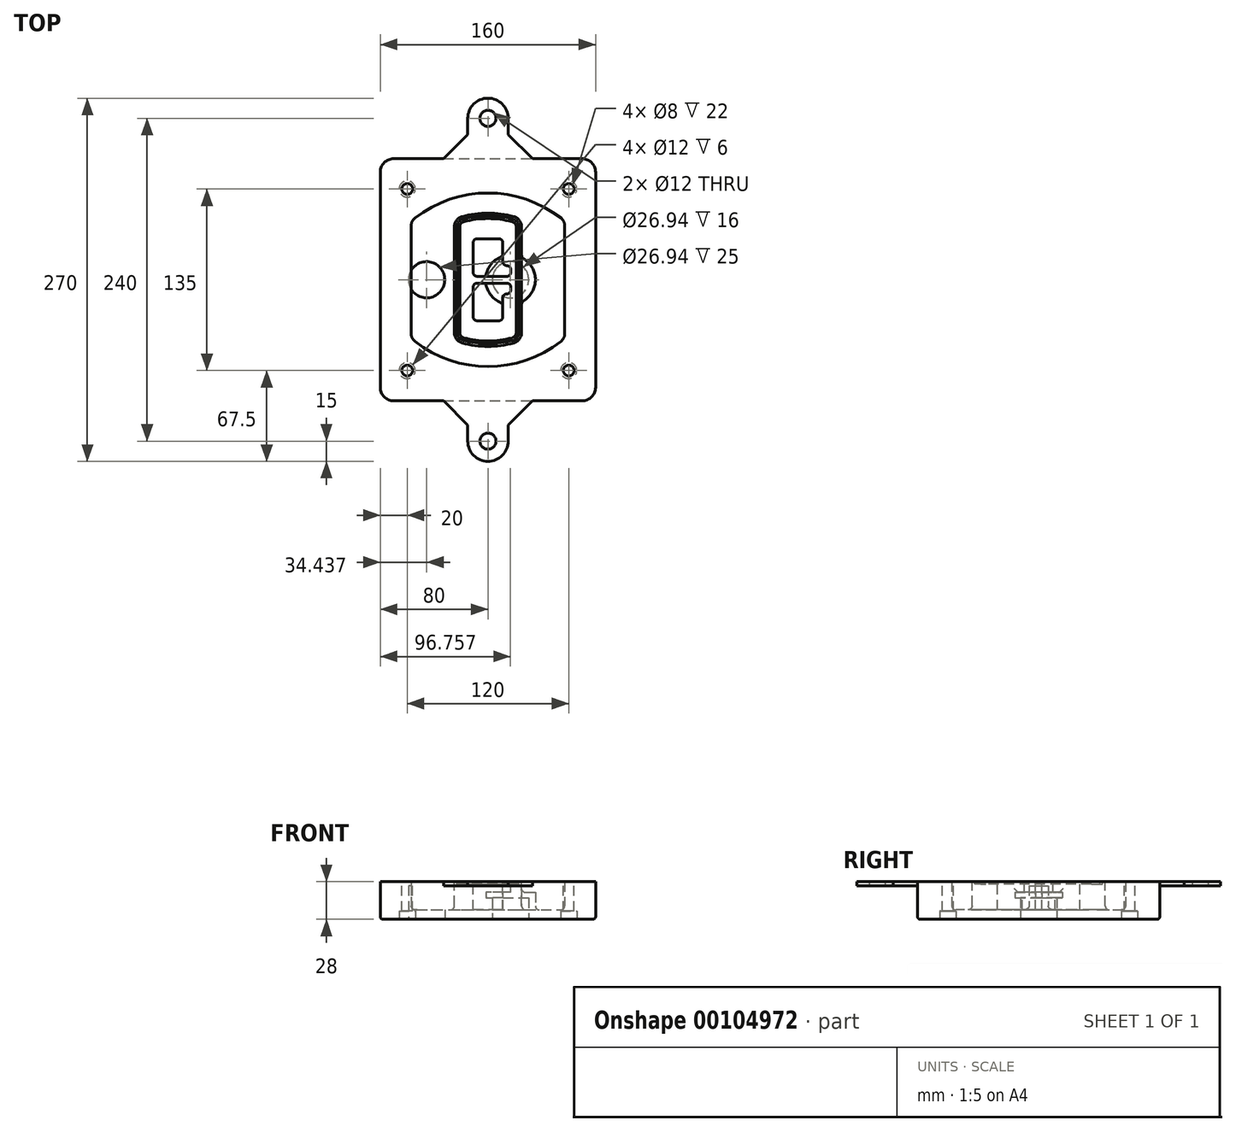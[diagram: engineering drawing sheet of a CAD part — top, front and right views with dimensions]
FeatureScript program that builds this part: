
annotation { "Feature Type Name" : "Feature", "Feature Type Description" : "" }
export const myFeature = defineFeature(function(context is Context, id is Id, definition is map)
    precondition{}
    {
        {
            var Q0;
            Q0=qCreatedBy(makeId("Top.planeOp"),FACE);
            var sketch = newSketch(context, id + "F0", { "sketchPlane" : qUnion([Q0])});
            skPoint(sketch, "E0.rect.middle", {"position": v(0, 0) * mm});
            skLineSegment(sketch, "E1.bottom", {"start": v(-70, -90) * mm, "end": v(70, -90) * mm});
            skLineSegment(sketch, "E1.top", {"start": v(-70, 90) * mm, "end": v(70, 90) * mm});
            skLineSegment(sketch, "E1.left", {"start": v(-80, -80) * mm, "end": v(-80, 80) * mm});
            skLineSegment(sketch, "E1.right", {"start": v(80, -80) * mm, "end": v(80, 80) * mm});
            skLineSegment(sketch, "E2", {"start": v(-80, 90) * mm, "end": v(80, -90) * mm, "construction": true});
            skLineSegment(sketch, "E3", {"start": v(80, 90) * mm, "end": v(-80, -90) * mm, "construction": true});
            skCircle(sketch, "E4", {"center": v(-60, 67.5) * mm, "radius": 4 * mm});
            skCircle(sketch, "E5", {"center": v(60, 67.5) * mm, "radius": 4 * mm});
            skCircle(sketch, "E6", {"center": v(60, -67.5) * mm, "radius": 4 * mm});
            skCircle(sketch, "E7", {"center": v(-60, -67.5) * mm, "radius": 4 * mm});
            skLineSegment(sketch, "E8", {"start": v(-60, 67.5) * mm, "end": v(60, 67.5) * mm, "construction": true});
            skLineSegment(sketch, "E9", {"start": v(60, 67.5) * mm, "end": v(60, -67.5) * mm, "construction": true});
            skLineSegment(sketch, "E10", {"start": v(60, -67.5) * mm, "end": v(-60, -67.5) * mm, "construction": true});
            skLineSegment(sketch, "E11", {"start": v(-60, -67.5) * mm, "end": v(-60, 67.5) * mm, "construction": true});
            skLineSegment(sketch, "E12", {"start": v(-60, 40.3) * mm, "end": v(-60, -40.3) * mm});
            skLineSegment(sketch, "E13", {"start": v(60, 40.3) * mm, "end": v(60, -40.3) * mm});
            skArc(sketch, "E14", {"start": v(56.15, 48.18) * mm, "mid": v(0, 67.5) * mm, "end": v(-56.15, 48.18) * mm});
            skArc(sketch, "E15", {"start": v(-56.15, -48.18) * mm, "mid": v(0, -67.5) * mm, "end": v(56.15, -48.18) * mm});
            skLineSegment(sketch, "E16", {"start": v(-60, 0) * mm, "end": v(60, 0) * mm, "construction": true});
            skPoint(sketch, "E17.visualSharp", {"position": v(-60, -45) * mm});
            skArc(sketch, "E17.filletArc", {"start": v(-60, -40.3) * mm, "mid": v(-58.99, -44.68) * mm, "end": v(-56.15, -48.18) * mm});
            skPoint(sketch, "E18.visualSharp", {"position": v(-60, 45) * mm});
            skArc(sketch, "E18.filletArc", {"start": v(-56.15, 48.18) * mm, "mid": v(-58.99, 44.68) * mm, "end": v(-60, 40.3) * mm});
            skPoint(sketch, "E19.visualSharp", {"position": v(60, 45) * mm});
            skArc(sketch, "E19.filletArc", {"start": v(60, 40.3) * mm, "mid": v(58.99, 44.68) * mm, "end": v(56.15, 48.18) * mm});
            skPoint(sketch, "E20.visualSharp", {"position": v(60, -45) * mm});
            skArc(sketch, "E20.filletArc", {"start": v(56.15, -48.18) * mm, "mid": v(58.99, -44.68) * mm, "end": v(60, -40.3) * mm});
            skPoint(sketch, "E21.visualSharp", {"position": v(-80, 90) * mm});
            skArc(sketch, "E21.filletArc", {"start": v(-70, 90) * mm, "mid": v(-77.07, 87.07) * mm, "end": v(-80, 80) * mm});
            skPoint(sketch, "E22.visualSharp", {"position": v(80, 90) * mm});
            skArc(sketch, "E22.filletArc", {"start": v(80, 80) * mm, "mid": v(77.07, 87.07) * mm, "end": v(70, 90) * mm});
            skPoint(sketch, "E23.visualSharp", {"position": v(80, -90) * mm});
            skArc(sketch, "E23.filletArc", {"start": v(70, -90) * mm, "mid": v(77.07, -87.07) * mm, "end": v(80, -80) * mm});
            skPoint(sketch, "E24.visualSharp", {"position": v(-80, -90) * mm});
            skArc(sketch, "E24.filletArc", {"start": v(-80, -80) * mm, "mid": v(-77.07, -87.07) * mm, "end": v(-70, -90) * mm});
            skArc(sketch, "E25.0", {"start": v(57, 40.3) * mm, "mid": v(56.3, 43.36) * mm, "end": v(54.3, 45.81) * mm});
            skLineSegment(sketch, "E25.1", {"start": v(57, 40.3) * mm, "end": v(57, -40.3) * mm});
            skArc(sketch, "E25.2", {"start": v(54.3, -45.81) * mm, "mid": v(56.3, -43.36) * mm, "end": v(57, -40.3) * mm});
            skArc(sketch, "E25.3", {"start": v(-54.3, -45.81) * mm, "mid": v(0, -64.5) * mm, "end": v(54.3, -45.81) * mm});
            skArc(sketch, "E25.4", {"start": v(-57, -40.3) * mm, "mid": v(-56.3, -43.36) * mm, "end": v(-54.3, -45.81) * mm});
            skArc(sketch, "E25.5", {"start": v(54.3, 45.81) * mm, "mid": v(0, 64.5) * mm, "end": v(-54.3, 45.81) * mm});
            skLineSegment(sketch, "E25.6", {"start": v(-57, 40.3) * mm, "end": v(-57, -40.3) * mm});
            skArc(sketch, "E25.7", {"start": v(-54.3, 45.81) * mm, "mid": v(-56.3, 43.36) * mm, "end": v(-57, 40.3) * mm});
            skArc(sketch, "E26.0", {"start": v(-58.62, 51.33) * mm, "mid": v(-62.58, 46.43) * mm, "end": v(-64, 40.3) * mm});
            skArc(sketch, "E26.1", {"start": v(58.62, 51.33) * mm, "mid": v(0, 71.5) * mm, "end": v(-58.62, 51.33) * mm});
            skArc(sketch, "E26.2", {"start": v(64, 40.3) * mm, "mid": v(62.58, 46.43) * mm, "end": v(58.62, 51.33) * mm});
            skLineSegment(sketch, "E26.3", {"start": v(64, 40.3) * mm, "end": v(64, -40.3) * mm});
            skArc(sketch, "E26.4", {"start": v(58.62, -51.33) * mm, "mid": v(62.58, -46.43) * mm, "end": v(64, -40.3) * mm});
            skLineSegment(sketch, "E26.5", {"start": v(-64, 40.3) * mm, "end": v(-64, -40.3) * mm});
            skArc(sketch, "E26.6", {"start": v(-58.62, -51.33) * mm, "mid": v(0, -71.5) * mm, "end": v(58.62, -51.33) * mm});
            skArc(sketch, "E26.7", {"start": v(-64, -40.3) * mm, "mid": v(-62.58, -46.43) * mm, "end": v(-58.62, -51.33) * mm});
            skSolve(sketch);
        }
        {
            var Q0;
            Q0=makeQuery(id+"F0.imprint","IMPRINT",FACE,{"disambiguationData":[TD([[makeQuery(id+"F0.imprint","IMPRINT",EDGE,{"derivedFrom":sQuery(id+"F0.wireOp",EDGE,"E1.bottom")}),1.0]])]});
            var Q1;
            Q1=makeQuery(id+"F0.imprint","IMPRINT",FACE,{"disambiguationData":[TD([[makeQuery(id+"F0.imprint","IMPRINT",EDGE,{"derivedFrom":sQuery(id+"F0.wireOp",EDGE,"E12")}),1.0]])]});
            var Q2;
            Q2=makeQuery(id+"F0.imprint","IMPRINT",FACE,{"disambiguationData":[TD([[makeQuery(id+"F0.imprint","IMPRINT",EDGE,{"derivedFrom":sQuery(id+"F0.wireOp",EDGE,"E25.0")}),1.0]])]});
            var Q3;
            Q3=makeQuery(id+"F0.imprint","IMPRINT",FACE,{"disambiguationData":[TD([[makeQuery(id+"F0.imprint","IMPRINT",EDGE,{"derivedFrom":sQuery(id+"F0.wireOp",EDGE,"E12")}),-1.0]])]});
            extrude(context, id + "F1", {"entities" : qUnion([Q0, Q1, Q2, Q3]), "oppositeDirection" : true, "depth" : 25 * mm});
        }
        {
            var Q0;
            Q0=makeQuery(id+"F0.imprint","IMPRINT",FACE,{"disambiguationData":[TD([[makeQuery(id+"F0.imprint","IMPRINT",EDGE,{"derivedFrom":sQuery(id+"F0.wireOp",EDGE,"E12")}),1.0]])]});
            extrude(context, id + "F2", {"entities" : qUnion([Q0]), "operationType" : NewBodyOperationType.ADD, "depth" : 3 * mm});
        }
        {
            var Q0;
            Q0=makeQuery(id+"F0.imprint","IMPRINT",FACE,{"disambiguationData":[TD([[makeQuery(id+"F0.imprint","IMPRINT",EDGE,{"derivedFrom":sQuery(id+"F0.wireOp",EDGE,"E25.0")}),1.0]])]});
            extrude(context, id + "F3", {"entities" : qUnion([Q0]), "operationType" : NewBodyOperationType.REMOVE, "oppositeDirection" : true, "depth" : 18 * mm});
        }
        {
            var Q0;
            Q0=makeQuery(id+"F2.opExtrude","CAP_FACE",FACE,{"disambiguationData":[OSD([sQuery(id+"F0.wireOp",EDGE,"E12"),sQuery(id+"F0.wireOp",EDGE,"E13"),sQuery(id+"F0.wireOp",EDGE,"E14"),sQuery(id+"F0.wireOp",EDGE,"E15"),sQuery(id+"F0.wireOp",EDGE,"E17.filletArc"),sQuery(id+"F0.wireOp",EDGE,"E18.filletArc"),sQuery(id+"F0.wireOp",EDGE,"E19.filletArc"),sQuery(id+"F0.wireOp",EDGE,"E20.filletArc"),sQuery(id+"F0.wireOp",EDGE,"E25.0"),sQuery(id+"F0.wireOp",EDGE,"E25.1"),sQuery(id+"F0.wireOp",EDGE,"E25.2"),sQuery(id+"F0.wireOp",EDGE,"E25.3"),sQuery(id+"F0.wireOp",EDGE,"E25.4"),sQuery(id+"F0.wireOp",EDGE,"E25.5"),sQuery(id+"F0.wireOp",EDGE,"E25.6"),sQuery(id+"F0.wireOp",EDGE,"E25.7")])],"isStart":false});
            var sketch = newSketch(context, id + "F4", { "sketchPlane" : qUnion([Q0])});
            skArc(sketch, "E27.0", {"start": v(-19.08, -46.97) * mm, "mid": v(0, -49.5) * mm, "end": v(19.08, -46.97) * mm});
            skArc(sketch, "E28.0", {"start": v(19.08, 46.97) * mm, "mid": v(0, 49.5) * mm, "end": v(-19.08, 46.97) * mm});
            skLineSegment(sketch, "E29", {"start": v(-25, 39.25) * mm, "end": v(-25, -39.25) * mm});
            skLineSegment(sketch, "E30", {"start": v(25, 39.25) * mm, "end": v(25, -39.25) * mm});
            skLineSegment(sketch, "E31", {"start": v(-25, 45.1) * mm, "end": v(25, 45.1) * mm, "construction": true});
            skLineSegment(sketch, "E32", {"start": v(-25, -45.1) * mm, "end": v(25, -45.1) * mm, "construction": true});
            skPoint(sketch, "E33.visualSharp", {"position": v(-25, 45.1) * mm});
            skArc(sketch, "E33.filletArc", {"start": v(-19.08, 46.97) * mm, "mid": v(-23.35, 44.11) * mm, "end": v(-25, 39.25) * mm});
            skPoint(sketch, "E34.visualSharp", {"position": v(25, 45.1) * mm});
            skArc(sketch, "E34.filletArc", {"start": v(25, 39.25) * mm, "mid": v(23.35, 44.11) * mm, "end": v(19.08, 46.97) * mm});
            skPoint(sketch, "E35.visualSharp", {"position": v(25, -45.1) * mm});
            skArc(sketch, "E35.filletArc", {"start": v(19.08, -46.97) * mm, "mid": v(23.35, -44.11) * mm, "end": v(25, -39.25) * mm});
            skPoint(sketch, "E36.visualSharp", {"position": v(-25, -45.1) * mm});
            skArc(sketch, "E36.filletArc", {"start": v(-25, -39.25) * mm, "mid": v(-23.35, -44.11) * mm, "end": v(-19.08, -46.97) * mm});
            skArc(sketch, "E37.0", {"start": v(54.3, 45.81) * mm, "mid": v(0, 64.5) * mm, "end": v(-54.3, 45.81) * mm});
            skArc(sketch, "E37.1", {"start": v(-54.3, 45.81) * mm, "mid": v(-56.3, 43.36) * mm, "end": v(-57, 40.3) * mm});
            skLineSegment(sketch, "E37.2", {"start": v(-57, 40.3) * mm, "end": v(-57, -40.3) * mm});
            skArc(sketch, "E37.3", {"start": v(-57, -40.3) * mm, "mid": v(-56.3, -43.36) * mm, "end": v(-54.3, -45.81) * mm});
            skArc(sketch, "E37.4", {"start": v(-54.3, -45.81) * mm, "mid": v(0, -64.5) * mm, "end": v(54.3, -45.81) * mm});
            skArc(sketch, "E37.5", {"start": v(54.3, -45.81) * mm, "mid": v(56.3, -43.36) * mm, "end": v(57, -40.3) * mm});
            skLineSegment(sketch, "E37.6", {"start": v(57, 40.3) * mm, "end": v(57, -40.3) * mm});
            skArc(sketch, "E37.7", {"start": v(57, 40.3) * mm, "mid": v(56.3, 43.36) * mm, "end": v(54.3, 45.81) * mm});
            skLineSegment(sketch, "E38.0", {"start": v(23, 39.25) * mm, "end": v(23, -39.25) * mm});
            skArc(sketch, "E38.1", {"start": v(18.56, -45.04) * mm, "mid": v(21.76, -42.9) * mm, "end": v(23, -39.25) * mm});
            skArc(sketch, "E38.2", {"start": v(-18.56, -45.04) * mm, "mid": v(0, -47.5) * mm, "end": v(18.56, -45.04) * mm});
            skArc(sketch, "E38.3", {"start": v(-23, -39.25) * mm, "mid": v(-21.76, -42.9) * mm, "end": v(-18.56, -45.04) * mm});
            skLineSegment(sketch, "E38.4", {"start": v(-23, 39.25) * mm, "end": v(-23, -39.25) * mm});
            skArc(sketch, "E38.5", {"start": v(23, 39.25) * mm, "mid": v(21.76, 42.9) * mm, "end": v(18.56, 45.04) * mm});
            skArc(sketch, "E38.6", {"start": v(-18.56, 45.04) * mm, "mid": v(-21.76, 42.9) * mm, "end": v(-23, 39.25) * mm});
            skArc(sketch, "E38.7", {"start": v(18.56, 45.04) * mm, "mid": v(0, 47.5) * mm, "end": v(-18.56, 45.04) * mm});
            skArc(sketch, "E39.0", {"start": v(21, 39.25) * mm, "mid": v(20.18, 41.68) * mm, "end": v(18.04, 43.1) * mm});
            skLineSegment(sketch, "E39.1", {"start": v(21, 39.25) * mm, "end": v(21, -39.25) * mm});
            skArc(sketch, "E39.2", {"start": v(18.04, -43.1) * mm, "mid": v(20.18, -41.68) * mm, "end": v(21, -39.25) * mm});
            skArc(sketch, "E39.3", {"start": v(-18.04, -43.1) * mm, "mid": v(0, -45.5) * mm, "end": v(18.04, -43.1) * mm});
            skArc(sketch, "E39.4", {"start": v(-21, -39.25) * mm, "mid": v(-20.18, -41.68) * mm, "end": v(-18.04, -43.1) * mm});
            skArc(sketch, "E39.5", {"start": v(18.04, 43.1) * mm, "mid": v(0, 45.5) * mm, "end": v(-18.04, 43.1) * mm});
            skLineSegment(sketch, "E39.6", {"start": v(-21, 39.25) * mm, "end": v(-21, -39.25) * mm});
            skArc(sketch, "E39.7", {"start": v(-18.04, 43.1) * mm, "mid": v(-20.18, 41.68) * mm, "end": v(-21, 39.25) * mm});
            skLineSegment(sketch, "E40", {"start": v(-25, 0) * mm, "end": v(25, 0) * mm, "construction": true});
            skLineSegment(sketch, "E41", {"start": v(-11, 5.5) * mm, "end": v(-11, 27.5) * mm});
            skLineSegment(sketch, "E42", {"start": v(-8, 30.5) * mm, "end": v(8, 30.5) * mm});
            skLineSegment(sketch, "E43", {"start": v(11, 27.5) * mm, "end": v(11, 13.5) * mm});
            skLineSegment(sketch, "E44", {"start": v(14, 10.5) * mm, "end": v(14, 10.5) * mm});
            skLineSegment(sketch, "E45", {"start": v(17, 7.5) * mm, "end": v(17, 5.5) * mm});
            skLineSegment(sketch, "E46", {"start": v(14, 2.5) * mm, "end": v(-8, 2.5) * mm});
            skPoint(sketch, "E47.visualSharp", {"position": v(-11, 30.5) * mm});
            skArc(sketch, "E47.filletArc", {"start": v(-8, 30.5) * mm, "mid": v(-10.12, 29.62) * mm, "end": v(-11, 27.5) * mm});
            skPoint(sketch, "E48.visualSharp", {"position": v(11, 30.5) * mm});
            skArc(sketch, "E48.filletArc", {"start": v(11, 27.5) * mm, "mid": v(10.12, 29.62) * mm, "end": v(8, 30.5) * mm});
            skPoint(sketch, "E49.visualSharp", {"position": v(11, 10.5) * mm});
            skArc(sketch, "E49.filletArc", {"start": v(11, 13.5) * mm, "mid": v(11.88, 11.38) * mm, "end": v(14, 10.5) * mm});
            skPoint(sketch, "E50.visualSharp", {"position": v(17, 10.5) * mm});
            skArc(sketch, "E50.filletArc", {"start": v(17, 7.5) * mm, "mid": v(16.12, 9.62) * mm, "end": v(14, 10.5) * mm});
            skPoint(sketch, "E51.visualSharp", {"position": v(17, 2.5) * mm});
            skArc(sketch, "E51.filletArc", {"start": v(14, 2.5) * mm, "mid": v(16.12, 3.38) * mm, "end": v(17, 5.5) * mm});
            skPoint(sketch, "E52.visualSharp", {"position": v(-11, 2.5) * mm});
            skArc(sketch, "E52.filletArc", {"start": v(-11, 5.5) * mm, "mid": v(-10.12, 3.38) * mm, "end": v(-8, 2.5) * mm});
            skLineSegment(sketch, "E53.0.MirrorCS", {"start": v(14, -2.5) * mm, "end": v(-8, -2.5) * mm});
            skArc(sketch, "E54.0.MirrorCS", {"start": v(-11, -5.5) * mm, "mid": v(-10.12, -3.38) * mm, "end": v(-8, -2.5) * mm});
            skLineSegment(sketch, "E55.0.MirrorCS", {"start": v(-11, -5.5) * mm, "end": v(-11, -27.5) * mm});
            skArc(sketch, "E56.0.MirrorCS", {"start": v(-8, -30.5) * mm, "mid": v(-10.12, -29.62) * mm, "end": v(-11, -27.5) * mm});
            skLineSegment(sketch, "E57.0.MirrorCS", {"start": v(-8, -30.5) * mm, "end": v(8, -30.5) * mm});
            skArc(sketch, "E58.0.MirrorCS", {"start": v(11, -27.5) * mm, "mid": v(10.12, -29.62) * mm, "end": v(8, -30.5) * mm});
            skLineSegment(sketch, "E59.0.MirrorCS", {"start": v(11, -27.5) * mm, "end": v(11, -13.5) * mm});
            skArc(sketch, "E60.0.MirrorCS", {"start": v(11, -13.5) * mm, "mid": v(11.88, -11.38) * mm, "end": v(14, -10.5) * mm});
            skArc(sketch, "E61.0.MirrorCS", {"start": v(17, -7.5) * mm, "mid": v(16.12, -9.62) * mm, "end": v(14, -10.5) * mm});
            skLineSegment(sketch, "E62.0.MirrorCS", {"start": v(17, -7.5) * mm, "end": v(17, -5.5) * mm});
            skArc(sketch, "E63.0.MirrorCS", {"start": v(14, -2.5) * mm, "mid": v(16.12, -3.38) * mm, "end": v(17, -5.5) * mm});
            skSolve(sketch);
        }
        {
            var Q0;
            Q0=makeQuery(id+"F4.imprint","IMPRINT",FACE,{"disambiguationData":[TD([[makeQuery(id+"F4.imprint","IMPRINT",EDGE,{"derivedFrom":sQuery(id+"F4.wireOp",EDGE,"E27.0")}),1.0]])]});
            var Q1;
            Q1=makeQuery(id+"F4.imprint","IMPRINT",FACE,{"disambiguationData":[TD([[makeQuery(id+"F4.imprint","IMPRINT",EDGE,{"derivedFrom":sQuery(id+"F4.wireOp",EDGE,"E38.0")}),-1.0]])]});
            var Q2;
            Q2=makeQuery(id+"F4.imprint","IMPRINT",FACE,{"disambiguationData":[TD([[makeQuery(id+"F4.imprint","IMPRINT",EDGE,{"derivedFrom":sQuery(id+"F4.wireOp",EDGE,"E39.0")}),1.0]])]});
            extrude(context, id + "F5", {"entities" : qUnion([Q0, Q1, Q2]), "operationType" : NewBodyOperationType.ADD, "endBound" : BoundingType.UP_TO_NEXT, "oppositeDirection" : true, "depth" : 25 * mm});
        }
        {
            var Q0;
            Q0=makeQuery(id+"F4.imprint","IMPRINT",FACE,{"disambiguationData":[TD([[makeQuery(id+"F4.imprint","IMPRINT",EDGE,{"derivedFrom":sQuery(id+"F4.wireOp",EDGE,"E38.0")}),-1.0]])]});
            extrude(context, id + "F6", {"entities" : qUnion([Q0]), "operationType" : NewBodyOperationType.REMOVE, "oppositeDirection" : true, "depth" : 2 * mm});
        }
        {
            var Q0;
            Q0=makeQuery(id+"F1.opExtrude","CAP_FACE",FACE,{"disambiguationData":[OSD([sQuery(id+"F0.wireOp",EDGE,"E1.bottom"),sQuery(id+"F0.wireOp",EDGE,"E1.top"),sQuery(id+"F0.wireOp",EDGE,"E1.left"),sQuery(id+"F0.wireOp",EDGE,"E1.right"),sQuery(id+"F0.wireOp",EDGE,"E4"),sQuery(id+"F0.wireOp",EDGE,"E5"),sQuery(id+"F0.wireOp",EDGE,"E6"),sQuery(id+"F0.wireOp",EDGE,"E7"),sQuery(id+"F0.wireOp",EDGE,"E21.filletArc"),sQuery(id+"F0.wireOp",EDGE,"E22.filletArc"),sQuery(id+"F0.wireOp",EDGE,"E23.filletArc"),sQuery(id+"F0.wireOp",EDGE,"E24.filletArc")])],"isStart":false});
            var sketch = newSketch(context, id + "F7", { "sketchPlane" : qUnion([Q0])});
            skCircle(sketch, "E64", {"center": v(16.76, 0) * mm, "radius": 13.47 * mm});
            skCircle(sketch, "E65", {"center": v(-45.56, 0) * mm, "radius": 13.47 * mm});
            skLineSegment(sketch, "E66", {"start": v(80, 0) * mm, "end": v(-80, 0) * mm});
            skCircle(sketch, "E67", {"center": v(16.76, 0) * mm, "radius": 18.47 * mm});
            skCircle(sketch, "E68", {"center": v(60, -67.5) * mm, "radius": 6 * mm});
            skCircle(sketch, "E69", {"center": v(-60, -67.5) * mm, "radius": 6 * mm});
            skCircle(sketch, "E70", {"center": v(-60, 67.5) * mm, "radius": 6 * mm});
            skCircle(sketch, "E71", {"center": v(60, 67.5) * mm, "radius": 6 * mm});
            skSolve(sketch);
        }
        {
            var Q0;
            {var subQ1=sQuery(id+"F7.wireOp",EDGE,"E66");var subQ4=sQuery(id+"F7.wireOp",EDGE,"E64");var subQ6=makeQuery(id+"F7.imprint","INTERSECT",VERTEX,{"disambiguationData":[OD(0.0)],"derivedFrom":[subQ4,subQ1]});Q0=makeQuery(id+"F7.imprint","IMPRINT",FACE,{"disambiguationData":[TD([[makeQuery(id+"F7.imprint","IMPRINT",EDGE,{"disambiguationData":[TD([[subQ6,-1.0]])],"derivedFrom":subQ4}),-1.0]])]});}
            var Q1;
            {var subQ0=sQuery(id+"F7.wireOp",EDGE,"E66");var subQ1=sQuery(id+"F7.wireOp",EDGE,"E64");var subQ3=makeQuery(id+"F7.imprint","INTERSECT",VERTEX,{"disambiguationData":[OD(0.0)],"derivedFrom":[subQ1,subQ0]});Q1=makeQuery(id+"F7.imprint","IMPRINT",FACE,{"disambiguationData":[TD([[makeQuery(id+"F7.imprint","IMPRINT",EDGE,{"disambiguationData":[TD([[subQ3,-1.0]])],"derivedFrom":subQ1}),1.0]])]});}
            var Q2;
            {var subQ0=sQuery(id+"F7.wireOp",EDGE,"E66");var subQ1=sQuery(id+"F7.wireOp",EDGE,"E64");var subQ3=makeQuery(id+"F7.imprint","INTERSECT",VERTEX,{"disambiguationData":[OD(0.0)],"derivedFrom":[subQ1,subQ0]});Q2=makeQuery(id+"F7.imprint","IMPRINT",FACE,{"disambiguationData":[TD([[makeQuery(id+"F7.imprint","IMPRINT",EDGE,{"disambiguationData":[TD([[subQ3,1.0]])],"derivedFrom":subQ1}),1.0]])]});}
            var Q3;
            {var subQ1=sQuery(id+"F7.wireOp",EDGE,"E66");var subQ4=sQuery(id+"F7.wireOp",EDGE,"E64");var subQ6=makeQuery(id+"F7.imprint","INTERSECT",VERTEX,{"disambiguationData":[OD(0.0)],"derivedFrom":[subQ4,subQ1]});Q3=makeQuery(id+"F7.imprint","IMPRINT",FACE,{"disambiguationData":[TD([[makeQuery(id+"F7.imprint","IMPRINT",EDGE,{"disambiguationData":[TD([[subQ6,1.0]])],"derivedFrom":subQ4}),-1.0]])]});}
            extrude(context, id + "F8", {"entities" : qUnion([Q0, Q1, Q2, Q3]), "operationType" : NewBodyOperationType.ADD, "oppositeDirection" : true, "depth" : 20 * mm});
        }
        {
            var Q0;
            {var subQ0=sQuery(id+"F7.wireOp",EDGE,"E66");var subQ1=sQuery(id+"F7.wireOp",EDGE,"E64");var subQ3=makeQuery(id+"F7.imprint","INTERSECT",VERTEX,{"disambiguationData":[OD(0.0)],"derivedFrom":[subQ1,subQ0]});Q0=makeQuery(id+"F7.imprint","IMPRINT",FACE,{"disambiguationData":[TD([[makeQuery(id+"F7.imprint","IMPRINT",EDGE,{"disambiguationData":[TD([[subQ3,-1.0]])],"derivedFrom":subQ1}),1.0]])]});}
            var Q1;
            {var subQ0=sQuery(id+"F7.wireOp",EDGE,"E66");var subQ1=sQuery(id+"F7.wireOp",EDGE,"E64");var subQ3=makeQuery(id+"F7.imprint","INTERSECT",VERTEX,{"disambiguationData":[OD(0.0)],"derivedFrom":[subQ1,subQ0]});Q1=makeQuery(id+"F7.imprint","IMPRINT",FACE,{"disambiguationData":[TD([[makeQuery(id+"F7.imprint","IMPRINT",EDGE,{"disambiguationData":[TD([[subQ3,1.0]])],"derivedFrom":subQ1}),1.0]])]});}
            extrude(context, id + "F9", {"entities" : qUnion([Q0, Q1]), "operationType" : NewBodyOperationType.REMOVE, "oppositeDirection" : true, "depth" : 16 * mm});
        }
        {
            var Q0;
            {var subQ0=sQuery(id+"F7.wireOp",EDGE,"E66");var subQ1=sQuery(id+"F7.wireOp",EDGE,"E65");var subQ3=makeQuery(id+"F7.imprint","INTERSECT",VERTEX,{"disambiguationData":[OD(0.0)],"derivedFrom":[subQ1,subQ0]});Q0=makeQuery(id+"F7.imprint","IMPRINT",FACE,{"disambiguationData":[TD([[makeQuery(id+"F7.imprint","IMPRINT",EDGE,{"disambiguationData":[TD([[subQ3,-1.0]])],"derivedFrom":subQ1}),1.0]])]});}
            var Q1;
            {var subQ0=sQuery(id+"F7.wireOp",EDGE,"E66");var subQ1=sQuery(id+"F7.wireOp",EDGE,"E65");var subQ3=makeQuery(id+"F7.imprint","INTERSECT",VERTEX,{"disambiguationData":[OD(0.0)],"derivedFrom":[subQ1,subQ0]});Q1=makeQuery(id+"F7.imprint","IMPRINT",FACE,{"disambiguationData":[TD([[makeQuery(id+"F7.imprint","IMPRINT",EDGE,{"disambiguationData":[TD([[subQ3,1.0]])],"derivedFrom":subQ1}),1.0]])]});}
            extrude(context, id + "F10", {"entities" : qUnion([Q0, Q1]), "operationType" : NewBodyOperationType.REMOVE, "oppositeDirection" : true, "depth" : 25 * mm});
        }
        {
            var Q0;
            Q0=makeQuery(id+"F7.imprint","IMPRINT",FACE,{"disambiguationData":[TD([[makeQuery(id+"F7.imprint","IMPRINT",EDGE,{"derivedFrom":sQuery(id+"F7.wireOp",EDGE,"E68")}),1.0]])]});
            var Q1;
            Q1=makeQuery(id+"F7.imprint","IMPRINT",FACE,{"disambiguationData":[TD([[makeQuery(id+"F7.imprint","IMPRINT",EDGE,{"derivedFrom":makeQuery(id+"F1.opExtrude","CAP_EDGE",EDGE,{"disambiguationData":[OSD([sQuery(id+"F0.wireOp",EDGE,"E5")])],"isStart":false})}),-1.0]])]});
            var Q2;
            Q2=makeQuery(id+"F7.imprint","IMPRINT",FACE,{"disambiguationData":[TD([[makeQuery(id+"F7.imprint","IMPRINT",EDGE,{"derivedFrom":sQuery(id+"F7.wireOp",EDGE,"E69")}),1.0]])]});
            var Q3;
            Q3=makeQuery(id+"F7.imprint","IMPRINT",FACE,{"disambiguationData":[TD([[makeQuery(id+"F7.imprint","IMPRINT",EDGE,{"derivedFrom":makeQuery(id+"F1.opExtrude","CAP_EDGE",EDGE,{"disambiguationData":[OSD([sQuery(id+"F0.wireOp",EDGE,"E4")])],"isStart":false})}),-1.0]])]});
            var Q4;
            Q4=makeQuery(id+"F7.imprint","IMPRINT",FACE,{"disambiguationData":[TD([[makeQuery(id+"F7.imprint","IMPRINT",EDGE,{"derivedFrom":sQuery(id+"F7.wireOp",EDGE,"E70")}),1.0]])]});
            var Q5;
            Q5=makeQuery(id+"F7.imprint","IMPRINT",FACE,{"disambiguationData":[TD([[makeQuery(id+"F7.imprint","IMPRINT",EDGE,{"derivedFrom":makeQuery(id+"F1.opExtrude","CAP_EDGE",EDGE,{"disambiguationData":[OSD([sQuery(id+"F0.wireOp",EDGE,"E7")])],"isStart":false})}),-1.0]])]});
            var Q6;
            Q6=makeQuery(id+"F7.imprint","IMPRINT",FACE,{"disambiguationData":[TD([[makeQuery(id+"F7.imprint","IMPRINT",EDGE,{"derivedFrom":sQuery(id+"F7.wireOp",EDGE,"E71")}),1.0]])]});
            var Q7;
            Q7=makeQuery(id+"F7.imprint","IMPRINT",FACE,{"disambiguationData":[TD([[makeQuery(id+"F7.imprint","IMPRINT",EDGE,{"derivedFrom":makeQuery(id+"F1.opExtrude","CAP_EDGE",EDGE,{"disambiguationData":[OSD([sQuery(id+"F0.wireOp",EDGE,"E6")])],"isStart":false})}),-1.0]])]});
            extrude(context, id + "F11", {"entities" : qUnion([Q0, Q1, Q2, Q3, Q4, Q5, Q6, Q7]), "operationType" : NewBodyOperationType.REMOVE, "oppositeDirection" : true, "depth" : 6 * mm});
        }
        {
            var Q0;
            Q0=makeQuery(id+"F9.boolean.opBoolean","COPY",FACE,{"derivedFrom":makeQuery(id+"F9.opExtrude","CAP_FACE",FACE,{"disambiguationData":[OSD([sQuery(id+"F7.wireOp",EDGE,"E64")])],"isStart":false})});
            var sketch = newSketch(context, id + "F12", { "sketchPlane" : qUnion([Q0])});
            skArc(sketch, "E72.0", {"start": v(11, 17.55) * mm, "mid": v(2.57, 11.82) * mm, "end": v(-1.54, 2.5) * mm});
            skArc(sketch, "E72.1", {"start": v(-1.54, -2.5) * mm, "mid": v(2.57, -11.82) * mm, "end": v(11, -17.55) * mm});
            skLineSegment(sketch, "E73", {"start": v(-1.54, -2.5) * mm, "end": v(14, -2.5) * mm});
            skLineSegment(sketch, "E74.0", {"start": v(14, 2.5) * mm, "end": v(-1.54, 2.5) * mm});
            skArc(sketch, "E74.1", {"start": v(14, 2.5) * mm, "mid": v(16.12, 3.38) * mm, "end": v(17, 5.5) * mm});
            skLineSegment(sketch, "E74.2", {"start": v(17, 7.5) * mm, "end": v(17, 5.5) * mm});
            skArc(sketch, "E74.3", {"start": v(17, 7.5) * mm, "mid": v(16.12, 9.62) * mm, "end": v(14, 10.5) * mm});
            skArc(sketch, "E74.4", {"start": v(11, 13.5) * mm, "mid": v(11.88, 11.38) * mm, "end": v(14, 10.5) * mm});
            skLineSegment(sketch, "E74.5", {"start": v(11, 17.55) * mm, "end": v(11, 13.5) * mm});
            skLineSegment(sketch, "E74.7", {"start": v(14, -2.5) * mm, "end": v(-1.54, -2.5) * mm});
            skArc(sketch, "E74.8", {"start": v(14, -2.5) * mm, "mid": v(16.12, -3.38) * mm, "end": v(17, -5.5) * mm});
            skLineSegment(sketch, "E74.9", {"start": v(17, -7.5) * mm, "end": v(17, -5.5) * mm});
            skArc(sketch, "E74.10", {"start": v(17, -7.5) * mm, "mid": v(16.12, -9.62) * mm, "end": v(14, -10.5) * mm});
            skArc(sketch, "E74.11", {"start": v(11, -13.5) * mm, "mid": v(11.88, -11.38) * mm, "end": v(14, -10.5) * mm});
            skLineSegment(sketch, "E74.12", {"start": v(11, -17.55) * mm, "end": v(11, -13.5) * mm});
            skPoint(sketch, "E75.orphan", {"position": v(11, -27.5) * mm});
            skPoint(sketch, "E76.orphan", {"position": v(-8, -2.5) * mm});
            skPoint(sketch, "E77.orphan", {"position": v(-8, 2.5) * mm});
            skPoint(sketch, "E78.orphan", {"position": v(11, 27.5) * mm});
            skSolve(sketch);
        }
        {
            var Q0;
            {var subQ7=sQuery(id+"F12.wireOp",EDGE,"E72.0");var subQ14=sQuery(id+"F12.wireOp",EDGE,"E72.1");var subQ16=sQuery(id+"F12.wireOp",EDGE,"E74.1");var subQ18=sQuery(id+"F12.wireOp",EDGE,"E74.8");Q0=qUnion([makeQuery(id+"F12.imprint","IMPRINT",FACE,{"disambiguationData":[TD([[makeQuery(id+"F12.imprint","IMPRINT",EDGE,{"derivedFrom":subQ7}),1.0]])]}),makeQuery(id+"F12.imprint","IMPRINT",FACE,{"disambiguationData":[TD([[makeQuery(id+"F12.imprint","IMPRINT",EDGE,{"derivedFrom":subQ14}),1.0]])]}),makeQuery(id+"F12.imprint","IMPRINT",FACE,{"disambiguationData":[TD([[makeQuery(id+"F12.imprint","IMPRINT",EDGE,{"derivedFrom":subQ16}),1.0]])]}),makeQuery(id+"F12.imprint","IMPRINT",FACE,{"disambiguationData":[TD([[makeQuery(id+"F12.imprint","IMPRINT",EDGE,{"derivedFrom":subQ18}),-1.0]])]})]);}
            var Q1;
            Q1=makeQuery(id+"F5.boolean.opBoolean","SPLIT",FACE,{"disambiguationData":[TD([makeQuery(id+"F5.opExtrude","SWEPT_FACE",FACE,{"disambiguationData":[OSD([sQuery(id+"F4.wireOp",EDGE,"E41")])]})])],"derivedFrom":makeQuery(id+"F3.boolean.opBoolean","COPY",FACE,{"derivedFrom":makeQuery(id+"F3.opExtrude","CAP_FACE",FACE,{"disambiguationData":[OSD([sQuery(id+"F0.wireOp",EDGE,"E25.0"),sQuery(id+"F0.wireOp",EDGE,"E25.1"),sQuery(id+"F0.wireOp",EDGE,"E25.2"),sQuery(id+"F0.wireOp",EDGE,"E25.3"),sQuery(id+"F0.wireOp",EDGE,"E25.4"),sQuery(id+"F0.wireOp",EDGE,"E25.5"),sQuery(id+"F0.wireOp",EDGE,"E25.6"),sQuery(id+"F0.wireOp",EDGE,"E25.7")])],"isStart":false})})});
            extrude(context, id + "F13", {"entities" : qUnion([Q0]), "operationType" : NewBodyOperationType.REMOVE, "endBound" : BoundingType.UP_TO_SURFACE, "endBoundEntityFace" : qUnion([Q1]), "depth" : 25 * mm});
        }
        {
            var Q0;
            Q0=makeQuery(id+"F3.boolean.opBoolean","COPY",EDGE,{"derivedFrom":makeQuery(id+"F3.opExtrude","CAP_EDGE",EDGE,{"disambiguationData":[OSD([sQuery(id+"F0.wireOp",EDGE,"E25.6")])],"isStart":false})});
            var Q1;
            Q1=makeQuery(id+"F8.boolean.opBoolean","INTERSECT",EDGE,{"derivedFrom":[makeQuery(id+"F5.opExtrude","SWEPT_FACE",FACE,{"disambiguationData":[OSD([sQuery(id+"F4.wireOp",EDGE,"E30")])]}),makeQuery(id+"F8.opExtrude","CAP_FACE",FACE,{"disambiguationData":[OSD([sQuery(id+"F7.wireOp",EDGE,"E67")])],"isStart":false})]});
            var Q2;
            Q2=makeQuery(id+"F8.boolean.opBoolean","INTERSECT",EDGE,{"disambiguationData":[OD(1.0)],"derivedFrom":[makeQuery(id+"F5.opExtrude","SWEPT_FACE",FACE,{"disambiguationData":[OSD([sQuery(id+"F4.wireOp",EDGE,"E30")])]}),makeQuery(id+"F8.opExtrude","SWEPT_FACE",FACE,{"disambiguationData":[OSD([sQuery(id+"F7.wireOp",EDGE,"E67")])]})]});
            var Q3;
            {var subQ0=sQuery(id+"F4.wireOp",EDGE,"E30");Q3=makeQuery(id+"F8.boolean.opBoolean","SPLIT",EDGE,{"disambiguationData":[TD([makeQuery(id+"F5.opExtrude","SWEPT_FACE",FACE,{"disambiguationData":[OSD([sQuery(id+"F4.wireOp",EDGE,"E35.filletArc")])]})])],"derivedFrom":makeQuery(id+"F5.opExtrude","CAP_EDGE",EDGE,{"disambiguationData":[OSD([subQ0])],"isStart":false})});}
            var Q4;
            {var subQ0=sQuery(id+"F0.wireOp",EDGE,"E25.7");var subQ1=sQuery(id+"F0.wireOp",EDGE,"E25.1");var subQ2=sQuery(id+"F0.wireOp",EDGE,"E25.6");var subQ3=sQuery(id+"F0.wireOp",EDGE,"E25.5");var subQ4=sQuery(id+"F0.wireOp",EDGE,"E25.4");var subQ5=sQuery(id+"F0.wireOp",EDGE,"E25.0");var subQ6=sQuery(id+"F0.wireOp",EDGE,"E25.2");var subQ7=sQuery(id+"F0.wireOp",EDGE,"E25.3");Q4=makeQuery(id+"F8.boolean.opBoolean","INTERSECT",EDGE,{"derivedFrom":[makeQuery(id+"F5.boolean.opBoolean","SPLIT",FACE,{"disambiguationData":[TD([makeQuery(id+"F2.opExtrude","SWEPT_FACE",FACE,{"disambiguationData":[OSD([subQ5])]})])],"derivedFrom":makeQuery(id+"F3.boolean.opBoolean","COPY",FACE,{"derivedFrom":makeQuery(id+"F3.opExtrude","CAP_FACE",FACE,{"disambiguationData":[OSD([subQ5,subQ1,subQ6,subQ7,subQ4,subQ3,subQ2,subQ0])],"isStart":false})})}),makeQuery(id+"F8.opExtrude","SWEPT_FACE",FACE,{"disambiguationData":[OSD([sQuery(id+"F7.wireOp",EDGE,"E67")])]})]});}
            var Q5;
            Q5=makeQuery(id+"F8.boolean.opBoolean","INTERSECT",EDGE,{"disambiguationData":[OD(0.0)],"derivedFrom":[makeQuery(id+"F5.opExtrude","SWEPT_FACE",FACE,{"disambiguationData":[OSD([sQuery(id+"F4.wireOp",EDGE,"E30")])]}),makeQuery(id+"F8.opExtrude","SWEPT_FACE",FACE,{"disambiguationData":[OSD([sQuery(id+"F7.wireOp",EDGE,"E67")])]})]});
            fillet(context, id + "F14", {"entities" : qUnion([Q0, Q1, Q2, Q3, Q4, Q5]), "radius" : 3 * mm, "tangentPropagation" : true, "allowEdgeOverflow" : false});
        }
        {
            var Q0;
            Q0=makeQuery(id+"F1.opExtrude","CAP_EDGE",EDGE,{"disambiguationData":[OSD([sQuery(id+"F0.wireOp",EDGE,"E1.bottom")])],"isStart":false});
            fillet(context, id + "F15", {"entities" : qUnion([Q0]), "radius" : 2 * mm, "tangentPropagation" : true, "allowEdgeOverflow" : false});
        }
        {
            var Q0;
            {var subQ0=sQuery(id+"F0.wireOp",EDGE,"E22.filletArc");var subQ1=sQuery(id+"F0.wireOp",EDGE,"E7");var subQ2=sQuery(id+"F0.wireOp",EDGE,"E6");var subQ3=sQuery(id+"F0.wireOp",EDGE,"E5");var subQ4=sQuery(id+"F0.wireOp",EDGE,"E4");var subQ5=sQuery(id+"F0.wireOp",EDGE,"E1.bottom");var subQ6=sQuery(id+"F0.wireOp",EDGE,"E21.filletArc");var subQ7=sQuery(id+"F0.wireOp",EDGE,"E1.top");var subQ8=sQuery(id+"F0.wireOp",EDGE,"E1.left");var subQ9=sQuery(id+"F0.wireOp",EDGE,"E1.right");var subQ10=sQuery(id+"F0.wireOp",EDGE,"E23.filletArc");var subQ11=sQuery(id+"F0.wireOp",EDGE,"E24.filletArc");Q0=makeQuery(id+"F2.boolean.opBoolean","SPLIT",FACE,{"disambiguationData":[TD([makeQuery(id+"F1.opExtrude","SWEPT_FACE",FACE,{"disambiguationData":[OSD([subQ5])]})])],"derivedFrom":makeQuery(id+"F1.opExtrude","CAP_FACE",FACE,{"disambiguationData":[OSD([subQ5,subQ7,subQ8,subQ9,subQ4,subQ3,subQ2,subQ1,subQ6,subQ0,subQ10,subQ11])],"isStart":true})});}
            var sketch = newSketch(context, id + "F16", { "sketchPlane" : qUnion([Q0])});
            skLineSegment(sketch, "E79", {"start": v(0, 90) * mm, "end": v(0, 120) * mm, "construction": true});
            skLineSegment(sketch, "E80", {"start": v(-33, 90) * mm, "end": v(-15, 108) * mm});
            skLineSegment(sketch, "E81", {"start": v(-15, 108) * mm, "end": v(-15, 120) * mm});
            skArc(sketch, "E82", {"start": v(15, 120) * mm, "mid": v(0, 135) * mm, "end": v(-15, 120) * mm});
            skLineSegment(sketch, "E83", {"start": v(15, 120) * mm, "end": v(15, 108) * mm});
            skLineSegment(sketch, "E84", {"start": v(15, 108) * mm, "end": v(33, 90) * mm});
            skCircle(sketch, "E85", {"center": v(0, 120) * mm, "radius": 6 * mm});
            skLineSegment(sketch, "E86", {"start": v(-80, 0) * mm, "end": v(80, 0) * mm});
            skLineSegment(sketch, "E87.MirrorCS", {"start": v(-33, -90) * mm, "end": v(-15, -108) * mm});
            skLineSegment(sketch, "E88.MirrorCS", {"start": v(-15, -108) * mm, "end": v(-15, -120) * mm});
            skArc(sketch, "E89.MirrorCS", {"start": v(15, -120) * mm, "mid": v(0, -135) * mm, "end": v(-15, -120) * mm});
            skCircle(sketch, "E90.MirrorC", {"center": v(0, -120) * mm, "radius": 6 * mm});
            skLineSegment(sketch, "E91.MirrorCS", {"start": v(0, -90) * mm, "end": v(0, -120) * mm, "construction": true});
            skLineSegment(sketch, "E92.MirrorCS", {"start": v(15, -120) * mm, "end": v(15, -108) * mm});
            skLineSegment(sketch, "E93.MirrorCS", {"start": v(15, -108) * mm, "end": v(33, -90) * mm});
            skSolve(sketch);
        }
        {
            var Q0;
            {var subQ0=sQuery(id+"F16.wireOp",EDGE,"E87.MirrorCS");Q0=makeQuery(id+"F16.imprint","IMPRINT",FACE,{"disambiguationData":[TD([[makeQuery(id+"F16.imprint","IMPRINT",EDGE,{"derivedFrom":subQ0}),1.0]])]});}
            var Q1;
            {var subQ0=sQuery(id+"F16.wireOp",EDGE,"E80");Q1=makeQuery(id+"F16.imprint","IMPRINT",FACE,{"disambiguationData":[TD([[makeQuery(id+"F16.imprint","IMPRINT",EDGE,{"derivedFrom":subQ0}),-1.0]])]});}
            var Q2;
            Q2=makeQuery(id+"F16.imprint","IMPRINT",FACE,{"disambiguationData":[TD([[makeQuery(id+"F16.imprint","IMPRINT",EDGE,{"derivedFrom":makeQuery(id+"F1.opExtrude","CAP_EDGE",EDGE,{"disambiguationData":[OSD([sQuery(id+"F0.wireOp",EDGE,"E6")])],"isStart":true})}),-1.0]])]});
            var Q3;
            Q3=makeQuery(id+"F16.imprint","IMPRINT",FACE,{"disambiguationData":[TD([[makeQuery(id+"F16.imprint","IMPRINT",EDGE,{"derivedFrom":makeQuery(id+"F1.opExtrude","CAP_EDGE",EDGE,{"disambiguationData":[OSD([sQuery(id+"F0.wireOp",EDGE,"E4")])],"isStart":true})}),-1.0]])]});
            var Q4;
            Q4=makeQuery(id+"F2.opExtrude","CAP_FACE",FACE,{"disambiguationData":[OSD([sQuery(id+"F0.wireOp",EDGE,"E12"),sQuery(id+"F0.wireOp",EDGE,"E13"),sQuery(id+"F0.wireOp",EDGE,"E14"),sQuery(id+"F0.wireOp",EDGE,"E15"),sQuery(id+"F0.wireOp",EDGE,"E17.filletArc"),sQuery(id+"F0.wireOp",EDGE,"E18.filletArc"),sQuery(id+"F0.wireOp",EDGE,"E19.filletArc"),sQuery(id+"F0.wireOp",EDGE,"E20.filletArc"),sQuery(id+"F0.wireOp",EDGE,"E25.0"),sQuery(id+"F0.wireOp",EDGE,"E25.1"),sQuery(id+"F0.wireOp",EDGE,"E25.2"),sQuery(id+"F0.wireOp",EDGE,"E25.3"),sQuery(id+"F0.wireOp",EDGE,"E25.4"),sQuery(id+"F0.wireOp",EDGE,"E25.5"),sQuery(id+"F0.wireOp",EDGE,"E25.6"),sQuery(id+"F0.wireOp",EDGE,"E25.7")])],"isStart":false});
            extrude(context, id + "F17", {"entities" : qUnion([Q0, Q1, Q2, Q3]), "operationType" : NewBodyOperationType.ADD, "endBound" : BoundingType.UP_TO_SURFACE, "endBoundEntityFace" : qUnion([Q4]), "depth" : 25 * mm});
        }
    });
